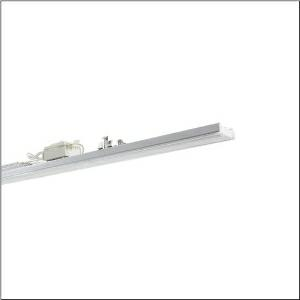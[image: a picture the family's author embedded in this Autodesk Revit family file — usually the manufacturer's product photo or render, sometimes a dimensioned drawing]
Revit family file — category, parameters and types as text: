
# Revit family: licross_11_recessed_mo_51te11mn4axg
name_source: partatom
category: Lighting Fixtures
units: mm (PartAtom-declared; Revit-internal decimal feet)

## family parameters
Cut with Voids When Loaded = No
Host = Face
Light Source = No
Part Type = Normal
Room Calculation Point = No
Round Connector Dimension = Use Diameter
Shared = No

## types (1)
- --- (1 x LED, 10130 lm, 55.2 W, 4000K)
    Apparent Load = 55 VA
    CIE Flux Codes = 89 96 99 100 100
    Color Rendering = 80
    Color Temperature = 4000K
    Default Elevation = 1800 mm
    Description = Licross 11 Recessed MO, luminaire insert, of sheet steel, galvanised, coil coated, white, length: 1.500mm, width: 66mm, height: 67mm, LED rated luminous flux: 10.130lm, light colour: 840, SDCM (Standard Deviation of Colour Matching)MacAdam ≤ 2 SDCM (initial), control gear: ON/OFF Multilumen, with plug, 3-pole, with phase selection, mains connection: 220..240V, AC, 50/60Hz, rated input power: 55W, internal wiring halogen-free, primary light control with lens, of plastic, primary optical cover: cover, of PMMA, light emission: direct distribution, primary light characteristic: symmetric, protection rating (complete): IP54, insulation class (complete): insulation class I (protective earthing), certification: CE, ENEC, VDE, UKCA, protection symbol: D if used in an environment with non-conductive dust loads with corresponding accessories, impact resistance: IK06, permissible ambient temperature for indoor applications: -35..+40°C, corresponds to IFS (International Featured Standards) requirements for safety and quality in the food industry, reducing of maximum allowable ambient temperature of 5°C with ceiling mounting, The light source and the operating device comply with the requirements of the Ecodesign Regulation (EU) 2019/2020 and are replaceable in accordance with this regulation, packaging unit: 1 piece
    Height = 58 mm
    Lamp = 1 x LED
    Lamp Light Flux = 10130 lm
    Lamp Power = 55.2 W
    Lamp count = 1
    Length = 1500 mm
    Luminous efficacy = 184 lm/W
    Manufacturer = Siteco
    ModVariant = No
    Model = 51TE11MN4AXG
    Mounting Place = Ceiling
    Mounting Type = Pendant
    Number of Poles = 1
    OnlyDefault = Yes
    Power Factor = 1
    Product Name = Licross 11 Recessed MO
    Product group = luminaire insert | ceiling pendant
    ProductGroupID = 901
    Protection Class = Protection class I
    Protection Degree = IP 54
    RLX_Detail_Level = 1
    RLX_Emergency_Light_Flux = 0 lm
    RLX_Emergency_Type = 0
    RLX_Emergency_Type_DB = No
    RlxData = <blob elided: 22425 chars, md5=088a8964>
    Socket = socket
    Standby Power = 0 W
    System Light Flux = 10130 lm
    System Power = 55 W
    Type Comments = factory setting: luminous flux: 100 % | (A | C | E) | 126 mA
    Type Image = l_1296930.jpg
    URL = http://relux.com
    VarID = @adj_089433
    Voltage = 0 V
    Weight = 0.00 kg
    Width = 66 mm

## geometry (parser evidence)
native form markers: Blend x4, Sweep x12
no freeform markers — native parametric forms only
